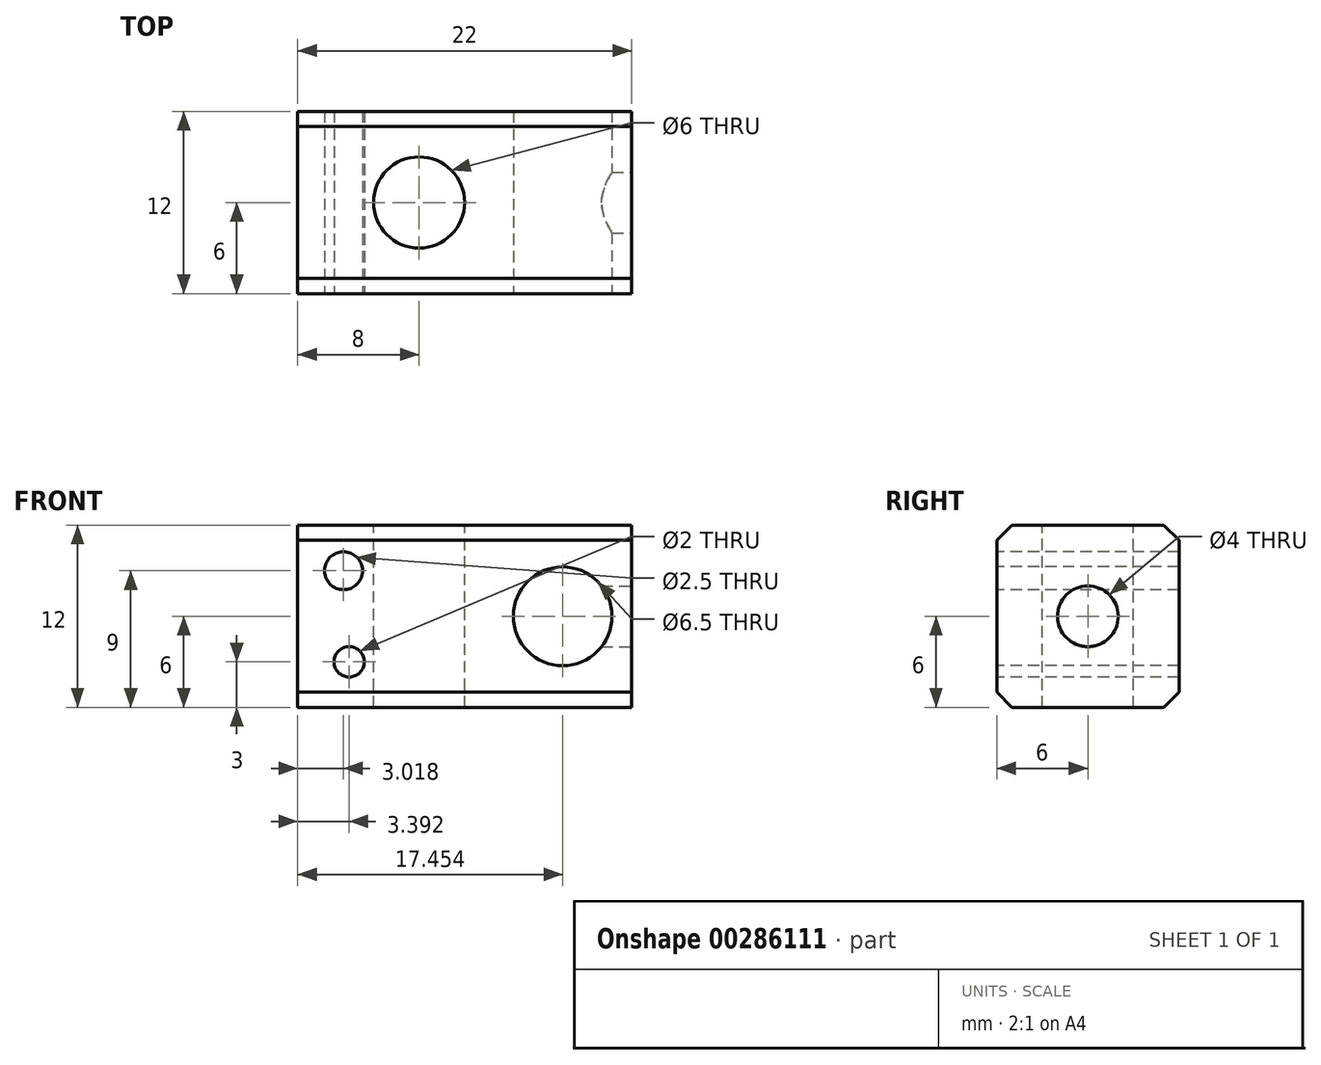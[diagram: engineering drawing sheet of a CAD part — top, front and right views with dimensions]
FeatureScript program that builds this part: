
annotation { "Feature Type Name" : "Feature", "Feature Type Description" : "" }
export const myFeature = defineFeature(function(context is Context, id is Id, definition is map)
    precondition{}
    {
        {
            var Q0;
            Q0=qCreatedBy(makeId("Top.planeOp"),FACE);
            var sketch = newSketch(context, id + "F0", { "sketchPlane" : qUnion([Q0])});
            skLineSegment(sketch, "E0.rect.bottom", {"start": v(11, 6) * mm, "end": v(-11, 6) * mm});
            skLineSegment(sketch, "E0.rect.top", {"start": v(11, -6) * mm, "end": v(-11, -6) * mm});
            skLineSegment(sketch, "E0.rect.left", {"start": v(11, 6) * mm, "end": v(11, -6) * mm});
            skLineSegment(sketch, "E0.rect.right", {"start": v(-11, 6) * mm, "end": v(-11, -6) * mm});
            skPoint(sketch, "E0.rect.middle", {"position": v(0, 0) * mm});
            skSolve(sketch);
        }
        {
            var Q0;
            Q0=qSketchRegion(id+"F0",true);
            extrude(context, id + "F1", {"entities" : qUnion([Q0]), "depth" : 12 * mm});
        }
        {
            var Q0;
            Q0=makeQuery(id+"F1.opExtrude","CAP_EDGE",EDGE,{"disambiguationData":[OSD([sQuery(id+"F0.wireOp",EDGE,"E0.rect.top")])],"isStart":false});
            var Q1;
            Q1=makeQuery(id+"F1.opExtrude","CAP_EDGE",EDGE,{"disambiguationData":[OSD([sQuery(id+"F0.wireOp",EDGE,"E0.rect.top")])],"isStart":true});
            var Q2;
            Q2=makeQuery(id+"F1.opExtrude","CAP_EDGE",EDGE,{"disambiguationData":[OSD([sQuery(id+"F0.wireOp",EDGE,"E0.rect.bottom")])],"isStart":true});
            var Q3;
            Q3=makeQuery(id+"F1.opExtrude","CAP_EDGE",EDGE,{"disambiguationData":[OSD([sQuery(id+"F0.wireOp",EDGE,"E0.rect.bottom")])],"isStart":false});
            chamfer(context, id + "F2", {"entities" : qUnion([Q0, Q1, Q2, Q3]), "width" : 1 * mm, "tangentPropagation" : true});
        }
        {
            var Q0;
            Q0=makeQuery(id+"F1.opExtrude","SWEPT_FACE",FACE,{"disambiguationData":[OSD([sQuery(id+"F0.wireOp",EDGE,"E0.rect.top")])]});
            var sketch = newSketch(context, id + "F3", { "sketchPlane" : qUnion([Q0])});
            skCircle(sketch, "E1", {"center": v(6.45, 6) * mm, "radius": 3.25 * mm});
            skCircle(sketch, "E2", {"center": v(-7.98, 9) * mm, "radius": 1.25 * mm});
            skCircle(sketch, "E3", {"center": v(-7.6, 3) * mm, "radius": 1 * mm});
            skSolve(sketch);
        }
        {
            var Q0;
            Q0=qSketchRegion(id+"F3",true);
            extrude(context, id + "F4", {"entities" : qUnion([Q0]), "operationType" : NewBodyOperationType.REMOVE, "endBound" : BoundingType.THROUGH_ALL, "oppositeDirection" : true, "depth" : 25 * mm});
        }
        {
            var Q0;
            Q0=makeQuery(id+"F1.opExtrude","SWEPT_FACE",FACE,{"disambiguationData":[OSD([sQuery(id+"F0.wireOp",EDGE,"E0.rect.left")])]});
            var sketch = newSketch(context, id + "F7", { "sketchPlane" : qUnion([Q0])});
            skCircle(sketch, "E4", {"center": v(0, 6) * mm, "radius": 2 * mm});
            skSolve(sketch);
        }
        {
            var Q0;
            Q0=qSketchRegion(id+"F7",true);
            extrude(context, id + "F5", {"entities" : qUnion([Q0]), "operationType" : NewBodyOperationType.REMOVE, "oppositeDirection" : true, "depth" : 4 * mm});
        }
        {
            var Q0;
            Q0=makeQuery(id+"F1.opExtrude","CAP_FACE",FACE,{"disambiguationData":[OSD([sQuery(id+"F0.wireOp",EDGE,"E0.rect.bottom"),sQuery(id+"F0.wireOp",EDGE,"E0.rect.top"),sQuery(id+"F0.wireOp",EDGE,"E0.rect.left"),sQuery(id+"F0.wireOp",EDGE,"E0.rect.right")])],"isStart":false});
            var sketch = newSketch(context, id + "F6", { "sketchPlane" : qUnion([Q0])});
            skCircle(sketch, "E5", {"center": v(-3, 0) * mm, "radius": 3 * mm});
            skSolve(sketch);
        }
        {
            var Q0;
            Q0=qSketchRegion(id+"F6",true);
            extrude(context, id + "F8", {"entities" : qUnion([Q0]), "operationType" : NewBodyOperationType.REMOVE, "oppositeDirection" : true, "depth" : 25 * mm});
        }
    });
